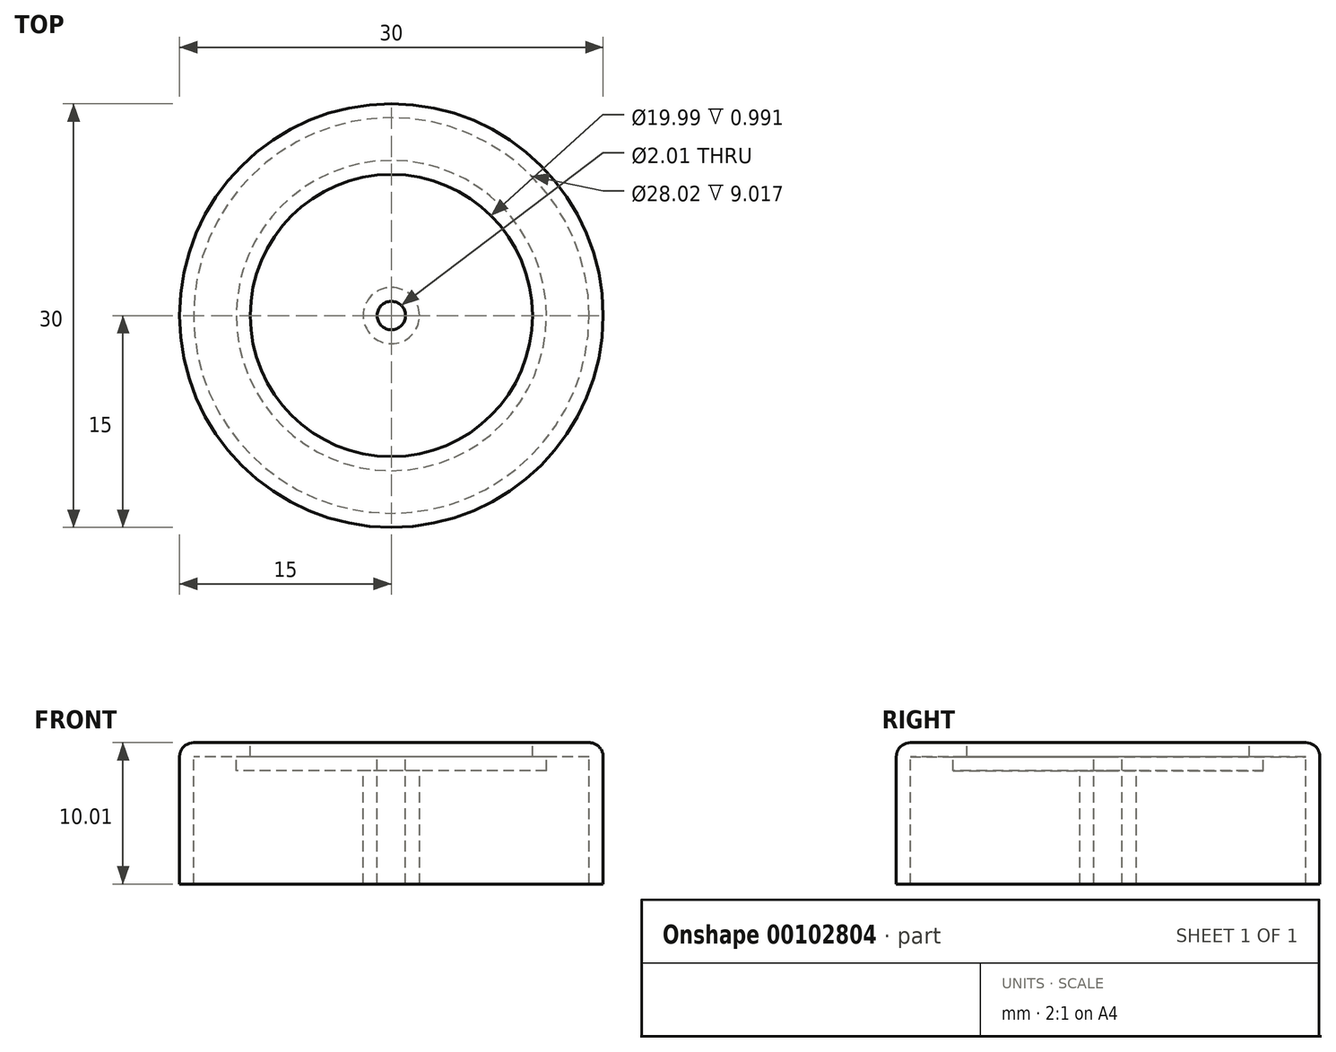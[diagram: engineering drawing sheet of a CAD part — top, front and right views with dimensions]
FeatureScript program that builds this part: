
annotation { "Feature Type Name" : "Feature", "Feature Type Description" : "" }
export const myFeature = defineFeature(function(context is Context, id is Id, definition is map)
    precondition{}
    {
        {
            var Q0;
            Q0=qCreatedBy(makeId("Top.planeOp"),FACE);
            var sketch = newSketch(context, id + "F0", { "sketchPlane" : qUnion([Q0])});
            skCircle(sketch, "E0", {"center": v(0, 0) * mm, "radius": 15 * mm});
            skSolve(sketch);
        }
        {
            var Q0;
            Q0=makeQuery(id+"F0.imprint","IMPRINT",FACE,{"disambiguationData":[TD([[makeQuery(id+"F0.imprint","IMPRINT",EDGE,{"derivedFrom":sQuery(id+"F0.wireOp",EDGE,"E0")}),1.0]])]});
            var Q1;
            Q1=sQuery(id+"F0.wireOp",EDGE,"E0");
            extrude(context, id + "F1", {"entities" : qUnion([Q0]), "surfaceEntities" : qUnion([Q1]), "oppositeDirection" : true, "depth" : 10 * mm});
        }
        {
            var Q0;
            Q0=makeQuery(id+"F1.opExtrude","CAP_FACE",FACE,{"disambiguationData":[OSD([sQuery(id+"F0.wireOp",EDGE,"E0")])],"isStart":true});
            var sketch = newSketch(context, id + "F2", { "sketchPlane" : qUnion([Q0])});
            skCircle(sketch, "E1", {"center": v(0, 0) * mm, "radius": 10 * mm});
            skSolve(sketch);
        }
        {
            var Q0;
            Q0=qSketchRegion(id+"F2",true);
            extrude(context, id + "F3", {"entities" : qUnion([Q0]), "operationType" : NewBodyOperationType.REMOVE, "oppositeDirection" : true, "depth" : 1 * mm});
        }
        {
            var Q0;
            Q0=qCreatedBy(makeId("Top.planeOp"),FACE);
            var sketch = newSketch(context, id + "F4", { "sketchPlane" : qUnion([Q0])});
            skCircle(sketch, "E2", {"center": v(0, 0) * mm, "radius": 1 * mm});
            skSolve(sketch);
        }
        {
            var Q0;
            Q0=qSketchRegion(id+"F4",true);
            extrude(context, id + "F5", {"entities" : qUnion([Q0]), "operationType" : NewBodyOperationType.REMOVE, "endBound" : BoundingType.THROUGH_ALL, "oppositeDirection" : true, "depth" : 25.4 * mm});
        }
        {
            var Q0;
            Q0=makeQuery(id+"F1.opExtrude","CAP_EDGE",EDGE,{"disambiguationData":[OSD([sQuery(id+"F0.wireOp",EDGE,"E0")])],"isStart":true});
            fillet(context, id + "F6", {"entities" : qUnion([Q0]), "radius" : 1 * mm, "tangentPropagation" : true, "allowEdgeOverflow" : false});
        }
        {
            var Q0;
            Q0=makeQuery(id+"F1.opExtrude","CAP_FACE",FACE,{"disambiguationData":[OSD([sQuery(id+"F0.wireOp",EDGE,"E0")])],"isStart":false});
            shell(context, id + "F7", {"entities" : qUnion([Q0]), "thickness" : 1 * mm});
        }
    });
